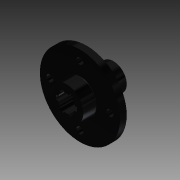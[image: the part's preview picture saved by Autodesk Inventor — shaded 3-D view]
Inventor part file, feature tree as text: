
AUTODESK INVENTOR PART (.ipt)
format: ipt  version: 2014 (Build 180170000, 170)  size: 203,776 bytes
history: native  units: mm (DEFAULTED — no unit token found)
features: sketch x8, extrude x5, hole x3, pattern_circular x2, fillet x1
ambient origin geometry x8: Origin, YZ Plane, XZ Plane, XY Plane, X Axis, Y Axis, Z Axis, Center Point
bodies: Solid1 (feature_tree)
feature tree (19):
  extrude  "Extrusion1"  Depth=6.35mm
  hole  "Mounting Hole"  [1 undecoded]
  pattern_circular  "Circular Pattern1"  Count=4 Angle=360.0deg
  extrude  "Extrusion2"  Depth=12.7mm TaperAngle=0.0deg
  hole  "Hole3"  [1 undecoded]
  extrude  "Extrusion3"  Depth=25.4mm
  pattern_circular  "Circular Pattern2"  [2 undecoded]
  extrude  "Extrusion4"  Depth=28.575mm TaperAngle=0.0deg
  extrude  "Extrusion5"  Depth=0.508mm
  hole  "Hole2"  [1 undecoded]
  fillet  "Fillet1"  Radius=4.0mm
  sketch  "Sketch1"  dims[d0=6.35mm d1=0.0mm d2=76.2mm]
  sketch  "Sketch2"  dims[d3=0.0mm d4=28.575mm]
  sketch  "Sketch3"  dims[d5=6.35mm d6=12.7mm d7=9.525mm d8=6.35mm d9=14.3117mm d10=19.05mm d11=20.594885mm d12=40.0mm d14=360.0deg]
  sketch  "Sketch4"  dims[d15=31.75mm d17=12.7mm d18=0.0mm]
  sketch  "Sketch5"  dims[d22=12.7mm d23=0.0mm d24=60.0mm d26=360.0deg]
  sketch  "Sketch6"  dims[d27=29.845mm d28=25.4mm d29=-0.872665mm]
  sketch  "Sketch7"  dims[d31=16.0mm]
  sketch  "Sketch8"  dims[d32=4.7625mm d33=10.31875mm d34=28.575mm d35=0.0mm d36=9.525mm d37=12.7mm d38=9.525mm d39=6.35mm d40=14.3117mm d41=19.05mm d42=20.594885mm d43=0.508mm d46=60.0deg d47=4.0mm d48=20.0mm d49=16.2mm d50=12.7mm d51=9.525mm d52=6.35mm d53=14.3117mm d54=14.986mm d55=0.0mm]
note: 5 required parameter values undecoded (feature->parameter linkage not recoverable at this tier; creation-order binding heuristic only, values carry confidence <= 0.55)
